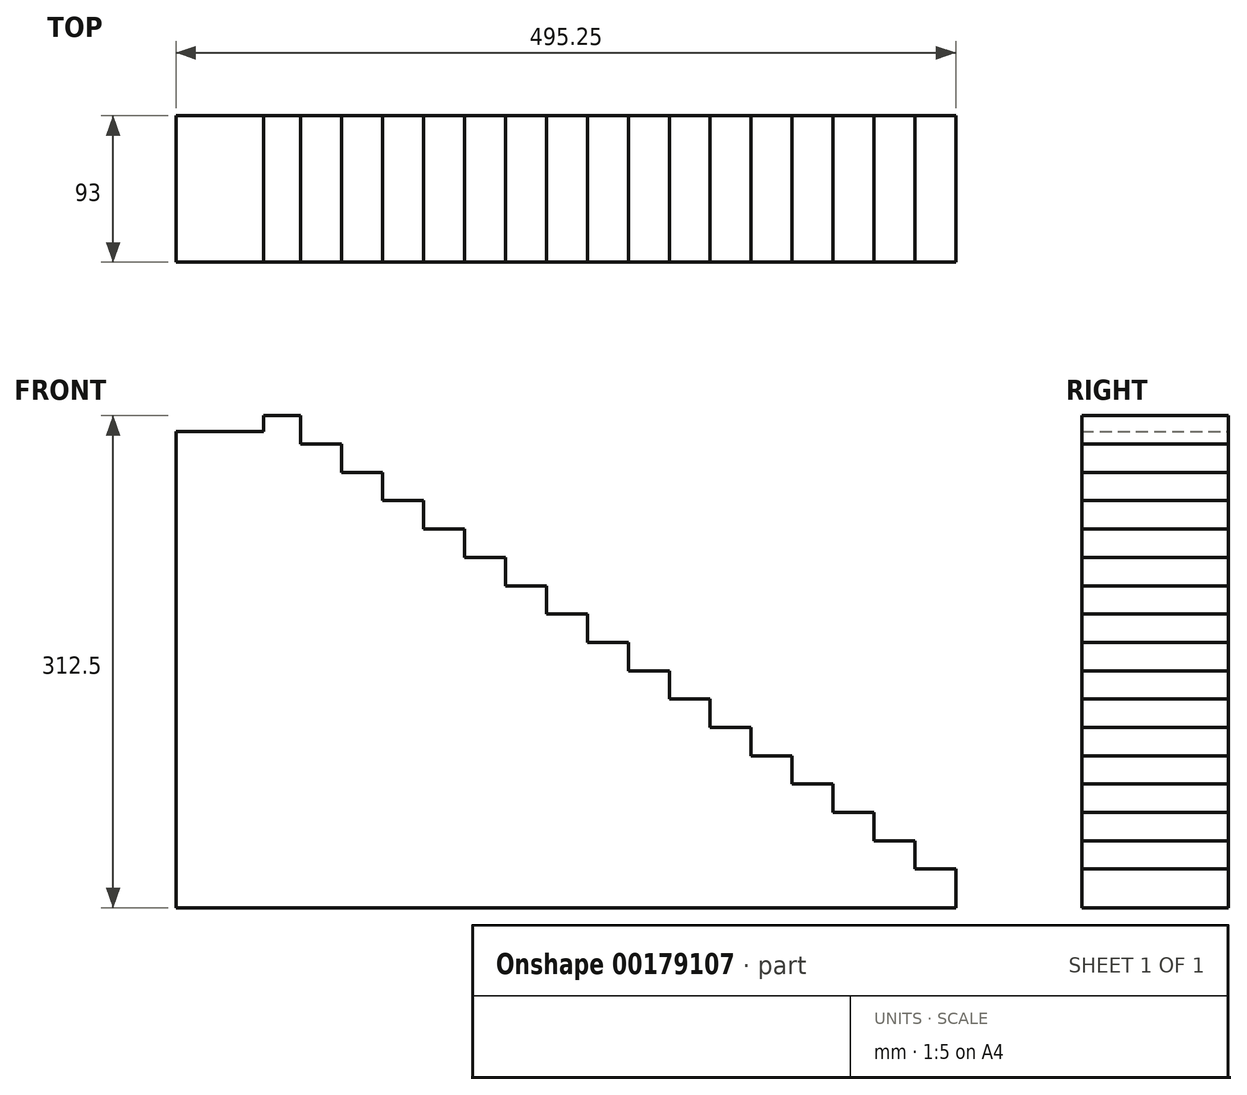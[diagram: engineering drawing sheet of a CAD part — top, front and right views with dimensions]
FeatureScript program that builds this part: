
annotation { "Feature Type Name" : "Feature", "Feature Type Description" : "" }
export const myFeature = defineFeature(function(context is Context, id is Id, definition is map)
    precondition{}
    {
        {
            var Q0;
            Q0=qCreatedBy(makeId("Front.planeOp"),FACE);
            var sketch = newSketch(context, id + "F0", { "sketchPlane" : qUnion([Q0])});
            skLineSegment(sketch, "E0", {"start": v(0, 0) * mm, "end": v(0, 0) * mm});
            skLineSegment(sketch, "E1", {"start": v(0, 0) * mm, "end": v(0, 9) * mm});
            skLineSegment(sketch, "E2", {"start": v(0, 24.5) * mm, "end": v(-26, 24.5) * mm});
            skLineSegment(sketch, "E3", {"start": v(-26, 42.5) * mm, "end": v(-52, 42.5) * mm});
            skLineSegment(sketch, "E4", {"start": v(-52, 42.5) * mm, "end": v(-52, 60.5) * mm});
            skLineSegment(sketch, "E5", {"start": v(-52, 60.5) * mm, "end": v(-78, 60.5) * mm});
            skLineSegment(sketch, "E6", {"start": v(-78, 60.5) * mm, "end": v(-78, 78.5) * mm});
            skLineSegment(sketch, "E7", {"start": v(-78, 78.5) * mm, "end": v(-104, 78.5) * mm});
            skLineSegment(sketch, "E8", {"start": v(-104, 78.5) * mm, "end": v(-104, 96.5) * mm});
            skLineSegment(sketch, "E9", {"start": v(-104, 96.5) * mm, "end": v(-130, 96.5) * mm});
            skLineSegment(sketch, "E10", {"start": v(-130, 96.5) * mm, "end": v(-130, 114.5) * mm});
            skLineSegment(sketch, "E11", {"start": v(-130, 114.5) * mm, "end": v(-156, 114.5) * mm});
            skLineSegment(sketch, "E12", {"start": v(-156, 114.5) * mm, "end": v(-156, 132.5) * mm});
            skLineSegment(sketch, "E13", {"start": v(-156, 132.5) * mm, "end": v(-182, 132.5) * mm});
            skLineSegment(sketch, "E14", {"start": v(-182, 132.5) * mm, "end": v(-182, 150.5) * mm});
            skLineSegment(sketch, "E15", {"start": v(-182, 150.5) * mm, "end": v(-208, 150.5) * mm});
            skLineSegment(sketch, "E16", {"start": v(-208, 150.5) * mm, "end": v(-208, 168.5) * mm});
            skLineSegment(sketch, "E17", {"start": v(-208, 168.5) * mm, "end": v(-234, 168.5) * mm});
            skLineSegment(sketch, "E18", {"start": v(-234, 168.5) * mm, "end": v(-234, 186.5) * mm});
            skLineSegment(sketch, "E19", {"start": v(-234, 186.5) * mm, "end": v(-260, 186.5) * mm});
            skLineSegment(sketch, "E20", {"start": v(-260, 186.5) * mm, "end": v(-260, 204.5) * mm});
            skLineSegment(sketch, "E21", {"start": v(-260, 204.5) * mm, "end": v(-286, 204.5) * mm});
            skLineSegment(sketch, "E22", {"start": v(-286, 204.5) * mm, "end": v(-286, 222.5) * mm});
            skLineSegment(sketch, "E23", {"start": v(-286, 222.5) * mm, "end": v(-312, 222.5) * mm});
            skLineSegment(sketch, "E24", {"start": v(-312, 222.5) * mm, "end": v(-312, 240.5) * mm});
            skLineSegment(sketch, "E25", {"start": v(-312, 240.5) * mm, "end": v(-338, 240.5) * mm});
            skLineSegment(sketch, "E26", {"start": v(-338, 240.5) * mm, "end": v(-338, 258.5) * mm});
            skLineSegment(sketch, "E27", {"start": v(-338, 258.5) * mm, "end": v(-364, 258.5) * mm});
            skLineSegment(sketch, "E28", {"start": v(-364, 258.5) * mm, "end": v(-364, 276.5) * mm});
            skLineSegment(sketch, "E29", {"start": v(-364, 276.5) * mm, "end": v(-390, 276.5) * mm});
            skLineSegment(sketch, "E30", {"start": v(-390, 276.5) * mm, "end": v(-390, 294.5) * mm});
            skLineSegment(sketch, "E31", {"start": v(-390, 294.5) * mm, "end": v(-416, 294.5) * mm});
            skLineSegment(sketch, "E32", {"start": v(0, 0) * mm, "end": v(-495.25, 0) * mm});
            skLineSegment(sketch, "E33", {"start": v(-495.25, 0) * mm, "end": v(-495.25, 302.5) * mm});
            skLineSegment(sketch, "E34", {"start": v(-416, 312.5) * mm, "end": v(113.16, 312.5) * mm});
            skLineSegment(sketch, "E35", {"start": v(-416, 294.5) * mm, "end": v(-416, 312.5) * mm});
            skLineSegment(sketch, "E36", {"start": v(-416, 312.5) * mm, "end": v(-439.65, 312.5) * mm});
            skLineSegment(sketch, "E37", {"start": v(-439.65, 312.5) * mm, "end": v(-439.65, 302.5) * mm});
            skLineSegment(sketch, "E38", {"start": v(-439.65, 302.5) * mm, "end": v(-495.25, 302.5) * mm});
            skLineSegment(sketch, "E39", {"start": v(0, 9) * mm, "end": v(63.08, 9) * mm});
            skLineSegment(sketch, "E40", {"start": v(0, 24.5) * mm, "end": v(0, 9) * mm});
            skLineSegment(sketch, "E41", {"start": v(-26, 42.5) * mm, "end": v(-26, 24.5) * mm});
            skSolve(sketch);
        }
        {
            var Q0;
            Q0=makeQuery(id+"F0.imprint","IMPRINT",FACE,{"disambiguationData":[TD([[makeQuery(id+"F0.imprint","IMPRINT",EDGE,{"derivedFrom":sQuery(id+"F0.wireOp",EDGE,"E1")}),1.0]])]});
            var Q1;
            Q1=makeQuery(id+"F0.imprint","IMPRINT",FACE,{"disambiguationData":[TD([[makeQuery(id+"F0.imprint","IMPRINT",EDGE,{"derivedFrom":sQuery(id+"F0.wireOp",EDGE,"E2")}),1.0]])]});
            extrude(context, id + "F1", {"entities" : qUnion([Q0, Q1]), "depth" : 93 * mm});
        }
    });
